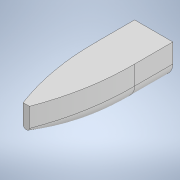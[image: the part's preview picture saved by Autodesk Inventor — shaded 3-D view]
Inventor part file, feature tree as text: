
AUTODESK INVENTOR PART (.ipt)
format: ipt  version: 2020.3 (Build 243373000, 373)  size: 219,136 bytes
history: native  units: mm
features: plane x4, sketch x3, extrude x1, loft x1, chamfer x1, other x1
ambient origin geometry x8: Origin, YZ Plane, XZ Plane, XY Plane, X Axis, Y Axis, Z Axis, Center Point
bodies: Solid1 (feature_tree)
feature tree (11):
  sketch  "Sketch1"  dims[d0=60.0mm d1=170.0mm]
  plane  "Work Plane1"
  plane  "Work Plane2"
  plane  "Work Plane3"
  plane  "Work Plane4"
  extrude  "Extrusion1"  Depth=170.0mm
  loft  "Loft3"
  chamfer  "Chamfer1"  Distance=30.0mm
  sketch  "Sketch3"  dims[d2=200.0mm d3=30.0mm]
  sketch  "Sketch4"  dims[d4=60.0mm d5=30.0mm d7=18.0mm d8=30.0mm d9=18.0mm d10=30.0mm d11=10.0mm d12=0.0mm d13=30.0mm d14=15.126927mm d16=9.076156mm d17=15.0mm d18=15.0mm d19=9.076156mm d24=10.0mm d25=5.0mm d26=3.0mm d27=3.0mm d28=5.0mm d29=5.0mm d35=0.0mm d36=90.0deg d37=0.0mm d38=90.0deg d39=0.0mm d40=90.0deg d42=2.0mm d43=2.0mm d44=45.0deg]
  other  "Edges3"
